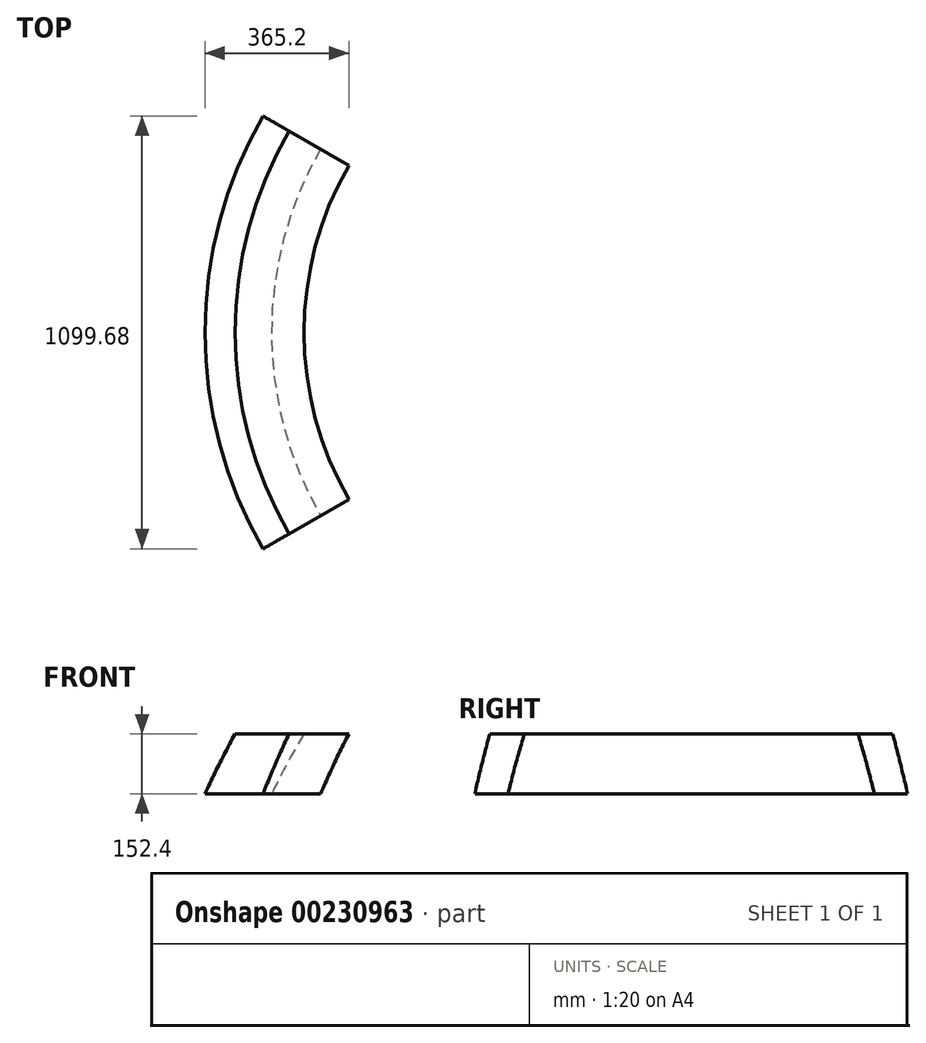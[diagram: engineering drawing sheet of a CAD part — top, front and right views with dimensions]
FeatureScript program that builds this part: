
annotation { "Feature Type Name" : "Feature", "Feature Type Description" : "" }
export const myFeature = defineFeature(function(context is Context, id is Id, definition is map)
    precondition{}
    {
        {
            var Q0;
            Q0=qCreatedBy(makeId("Front.planeOp"),FACE);
            var sketch = newSketch(context, id + "F0", { "sketchPlane" : qUnion([Q0])});
            skLineSegment(sketch, "E0", {"start": v(-1181.84, -1150.9) * mm, "end": v(-927.84, -1150.9) * mm});
            skFitSpline(sketch, "E1", {"points": [v(0, 1953.34) * mm, v(-1100.72, 1005.82) * mm, v(-1321.31, -446.03) * mm, v(-1216.83, -971.67) * mm, v(-1181.84, -1150.9) * mm], "startDerivative": vector(-4000.43, 5.06) * mm, "endDerivative": vector(0, -1489.55) * mm});
            skLineSegment(sketch, "E2", {"start": v(-1099.69, 1008.1) * mm, "end": v(-930.94, 1008.1) * mm});
            skLineSegment(sketch, "E3", {"start": v(-1181.84, -1150.9) * mm, "end": v(-1181.84, -1354.1) * mm});
            skLineSegment(sketch, "E4", {"start": v(-1181.84, -1354.1) * mm, "end": v(-877.04, -1354.1) * mm});
            skLineSegment(sketch, "E5", {"start": v(-877.04, -1354.1) * mm, "end": v(-877.04, -1252.5) * mm});
            skLineSegment(sketch, "E6", {"start": v(-877.04, -1252.5) * mm, "end": v(-927.84, -1252.5) * mm});
            skLineSegment(sketch, "E7", {"start": v(-927.84, -1252.5) * mm, "end": v(-927.84, -1150.9) * mm});
            skFitSpline(sketch, "E8.trimOffspring", {"points": [v(0, -1757.92) * mm, v(-927.84, -1150.9) * mm, v(-1179.31, -127.8) * mm, v(-917.89, 1034.08) * mm, v(0, 1800.66) * mm], "startDerivative": vector(-4973.2, 113.59) * mm, "endDerivative": vector(4756.7, 336.76) * mm});
            skLineSegment(sketch, "E9", {"start": v(-1023.33, 1160.5) * mm, "end": v(-848.12, 1160.5) * mm});
            skLineSegment(sketch, "E10", {"start": v(0, 1953.34) * mm, "end": v(0, 1800.66) * mm});
            skSolve(sketch);
        }
        {
            var Q0;
            {var subQ0=sQuery(id+"F0.wireOp",EDGE,"E2");Q0=makeQuery(id+"F0.imprint","IMPRINT",FACE,{"disambiguationData":[TD([[makeQuery(id+"F0.imprint","IMPRINT",EDGE,{"derivedFrom":subQ0}),1.0]])]});}
            var Q1;
            Q1=sQuery(id+"F0.wireOp",EDGE,"E10");
            revolve(context, id + "F1", {"entities" : qUnion([Q0]), "axis" : qUnion([Q1]), "revolveType" : RevolveType.SYMMETRIC, "angle" : 60 * degree});
        }
    });
